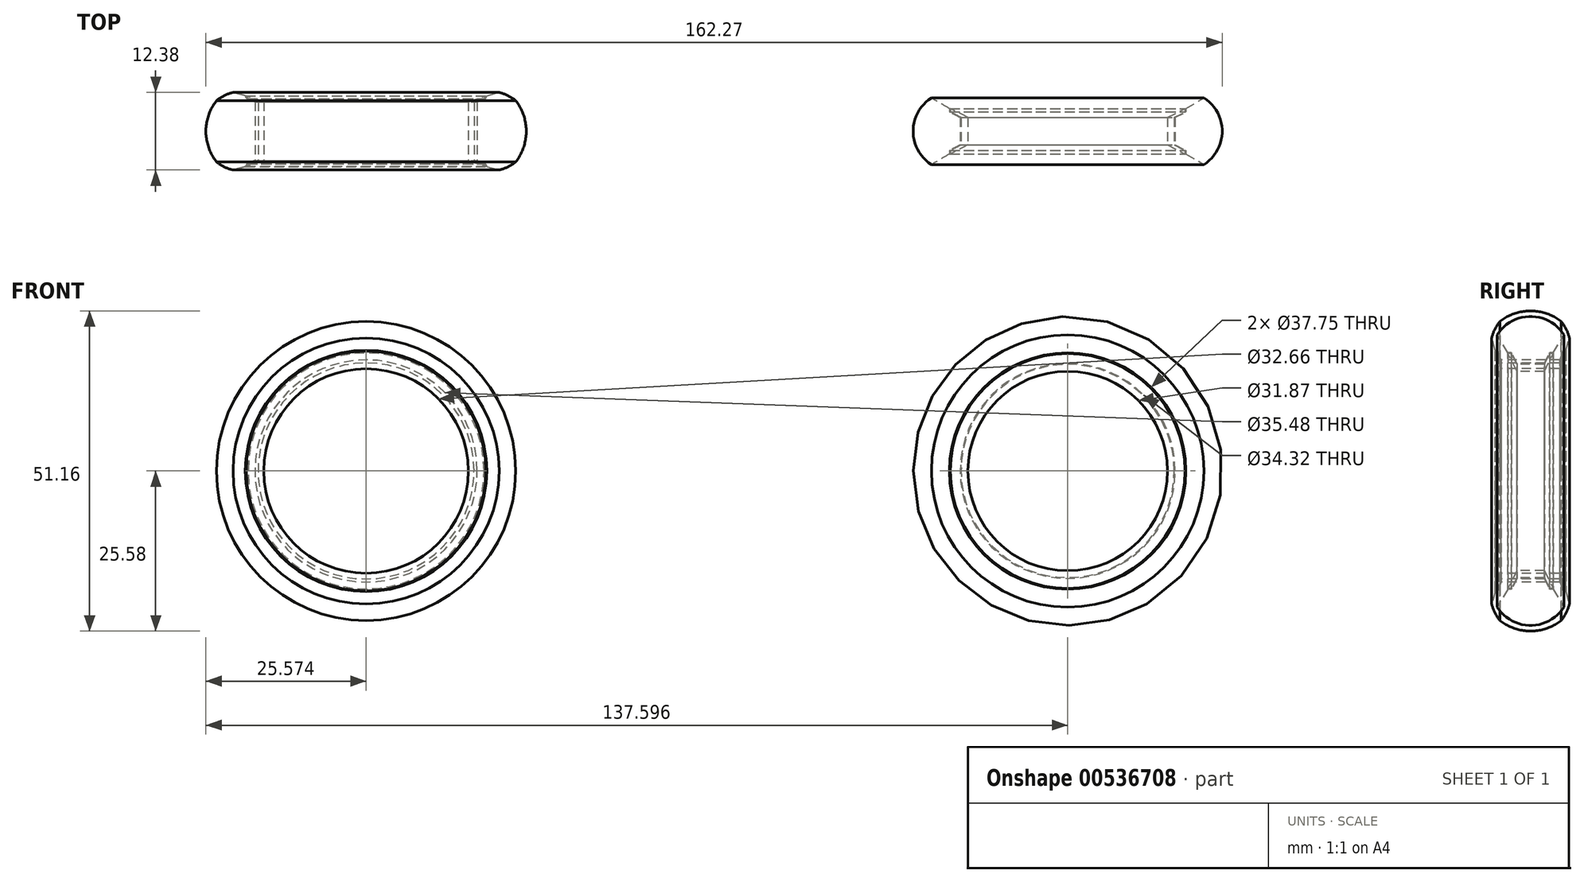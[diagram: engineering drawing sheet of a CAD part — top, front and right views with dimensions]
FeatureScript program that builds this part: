
annotation { "Feature Type Name" : "Feature", "Feature Type Description" : "" }
export const myFeature = defineFeature(function(context is Context, id is Id, definition is map)
    precondition{}
    {
        {
            var Q0;
            Q0=qCreatedBy(makeId("Right.planeOp"),FACE);
            var sketch = newSketch(context, id + "F0", { "sketchPlane" : qUnion([Q0])});
            skLineSegment(sketch, "E0", {"start": v(-44.75, 0) * mm, "end": v(51, 0) * mm, "construction": true});
            skLineSegment(sketch, "E1", {"start": v(-39.14, 41.52) * mm, "end": v(68.46, 41.52) * mm, "construction": true});
            skLineSegment(sketch, "E2", {"start": v(0, 87.56) * mm, "end": v(0, -13.22) * mm, "construction": true});
            skArc(sketch, "E3", {"start": v(5.33, 63.27) * mm, "mid": v(3.04, 65.41) * mm, "end": v(0, 66.19) * mm});
            skLineSegment(sketch, "E4", {"start": v(0, 58.68) * mm, "end": v(2.2, 58.68) * mm});
            skLineSegment(sketch, "E5", {"start": v(2.2, 58.68) * mm, "end": v(3.07, 60.4) * mm});
            skLineSegment(sketch, "E6", {"start": v(3.07, 60.4) * mm, "end": v(3.63, 60.4) * mm});
            skLineSegment(sketch, "E7", {"start": v(3.63, 60.4) * mm, "end": v(5.33, 63.27) * mm});
            skLineSegment(sketch, "E8", {"start": v(0, 58.54) * mm, "end": v(2.2, 58.54) * mm});
            skLineSegment(sketch, "E9", {"start": v(2.2, 58.54) * mm, "end": v(3.07, 60.25) * mm});
            skLineSegment(sketch, "E10", {"start": v(3.07, 60.25) * mm, "end": v(3.63, 60.25) * mm});
            skLineSegment(sketch, "E11", {"start": v(3.63, 60.25) * mm, "end": v(2.2, 57.45) * mm});
            skLineSegment(sketch, "E12", {"start": v(2.2, 57.45) * mm, "end": v(0, 57.45) * mm});
            skArc(sketch, "E13.MirrorCS", {"start": v(-5.33, 63.27) * mm, "mid": v(-3.04, 65.41) * mm, "end": v(0, 66.19) * mm});
            skLineSegment(sketch, "E14.MirrorCS", {"start": v(-3.07, 60.4) * mm, "end": v(-3.63, 60.4) * mm});
            skLineSegment(sketch, "E15.MirrorCS", {"start": v(-3.63, 60.4) * mm, "end": v(-5.33, 63.27) * mm});
            skLineSegment(sketch, "E16.MirrorCS", {"start": v(-3.07, 60.25) * mm, "end": v(-3.63, 60.25) * mm});
            skLineSegment(sketch, "E17.MirrorCS", {"start": v(-3.63, 60.25) * mm, "end": v(-2.2, 57.45) * mm});
            skLineSegment(sketch, "E18.MirrorCS", {"start": v(-2.2, 58.54) * mm, "end": v(-3.07, 60.25) * mm});
            skLineSegment(sketch, "E19.MirrorCS", {"start": v(-2.2, 58.68) * mm, "end": v(-3.07, 60.4) * mm});
            skLineSegment(sketch, "E20.MirrorCS", {"start": v(0, 58.68) * mm, "end": v(-2.2, 58.68) * mm});
            skLineSegment(sketch, "E21.MirrorCS", {"start": v(0, 58.54) * mm, "end": v(-2.2, 58.54) * mm});
            skLineSegment(sketch, "E22.MirrorCS", {"start": v(-2.2, 57.45) * mm, "end": v(0, 57.45) * mm});
            skLineSegment(sketch, "E23", {"start": v(-36.7, -39.4) * mm, "end": v(34, -39.4) * mm, "construction": true});
            skArc(sketch, "E24", {"start": v(6.2, -18.16) * mm, "mid": v(5.7, -16.76) * mm, "end": v(4.88, -15.5) * mm});
            skArc(sketch, "E25", {"start": v(4.88, -15.5) * mm, "mid": v(2.58, -14.27) * mm, "end": v(0, -13.83) * mm});
            skLineSegment(sketch, "E26", {"start": v(6.2, -18.16) * mm, "end": v(5.67, -20.13) * mm});
            skLineSegment(sketch, "E27", {"start": v(5.67, -20.13) * mm, "end": v(5.21, -20.35) * mm});
            skLineSegment(sketch, "E28", {"start": v(5.21, -20.35) * mm, "end": v(4.7, -21.66) * mm});
            skLineSegment(sketch, "E29", {"start": v(4.7, -21.66) * mm, "end": v(0, -21.66) * mm});
            skLineSegment(sketch, "E30", {"start": v(0, -22.16) * mm, "end": v(4.7, -22.16) * mm});
            skLineSegment(sketch, "E31", {"start": v(4.7, -22.16) * mm, "end": v(5.21, -20.57) * mm});
            skLineSegment(sketch, "E32", {"start": v(5.21, -20.57) * mm, "end": v(5.62, -20.27) * mm});
            skLineSegment(sketch, "E33", {"start": v(5.62, -20.27) * mm, "end": v(4.7, -23.08) * mm});
            skLineSegment(sketch, "E34", {"start": v(4.7, -23.08) * mm, "end": v(0, -23.08) * mm});
            skLineSegment(sketch, "E35.trimOffspring", {"start": v(0, -13.83) * mm, "end": v(0, -66.36) * mm, "construction": true});
            skArc(sketch, "E36.MirrorCS", {"start": v(-4.88, -15.5) * mm, "mid": v(-2.58, -14.27) * mm, "end": v(0, -13.83) * mm});
            skArc(sketch, "E37.MirrorCS", {"start": v(-6.2, -18.16) * mm, "mid": v(-5.7, -16.76) * mm, "end": v(-4.88, -15.5) * mm});
            skLineSegment(sketch, "E38.MirrorCS", {"start": v(-5.62, -20.27) * mm, "end": v(-4.7, -23.08) * mm});
            skLineSegment(sketch, "E39.MirrorCS", {"start": v(-4.7, -23.08) * mm, "end": v(0, -23.08) * mm});
            skLineSegment(sketch, "E40.MirrorCS", {"start": v(0, -22.16) * mm, "end": v(-4.7, -22.16) * mm});
            skLineSegment(sketch, "E41.MirrorCS", {"start": v(-4.7, -21.66) * mm, "end": v(0, -21.66) * mm});
            skLineSegment(sketch, "E42.MirrorCS", {"start": v(-6.2, -18.16) * mm, "end": v(-5.67, -20.13) * mm});
            skLineSegment(sketch, "E43.MirrorCS", {"start": v(-4.7, -22.16) * mm, "end": v(-5.21, -20.57) * mm});
            skLineSegment(sketch, "E44.MirrorCS", {"start": v(-5.21, -20.35) * mm, "end": v(-4.7, -21.66) * mm});
            skLineSegment(sketch, "E45.MirrorCS", {"start": v(-5.67, -20.13) * mm, "end": v(-5.21, -20.35) * mm});
            skLineSegment(sketch, "E46.MirrorCS", {"start": v(-5.21, -20.57) * mm, "end": v(-5.62, -20.27) * mm});
            skSolve(sketch);
        }
        {
            var Q0;
            Q0=makeQuery(id+"F0.imprint","IMPRINT",FACE,{"disambiguationData":[TD([[makeQuery(id+"F0.imprint","IMPRINT",EDGE,{"derivedFrom":sQuery(id+"F0.wireOp",EDGE,"E3")}),1.0]])]});
            var Q1;
            Q1=makeQuery(id+"F0.imprint","IMPRINT",FACE,{"disambiguationData":[TD([[makeQuery(id+"F0.imprint","IMPRINT",EDGE,{"derivedFrom":sQuery(id+"F0.wireOp",EDGE,"E8")}),-1.0]])]});
            var Q2;
            Q2=sQuery(id+"F0.wireOp",EDGE,"E1");
            revolve(context, id + "F1", {"entities" : qUnion([Q0, Q1]), "axis" : qUnion([Q2]), "revolveType" : RevolveType.FULL});
        }
        {
            var Q0;
            Q0=makeQuery(id+"F0.imprint","IMPRINT",FACE,{"disambiguationData":[TD([[makeQuery(id+"F0.imprint","IMPRINT",EDGE,{"derivedFrom":sQuery(id+"F0.wireOp",EDGE,"E24")}),1.0]])]});
            var Q1;
            Q1=makeQuery(id+"F0.imprint","IMPRINT",FACE,{"disambiguationData":[TD([[makeQuery(id+"F0.imprint","IMPRINT",EDGE,{"derivedFrom":sQuery(id+"F0.wireOp",EDGE,"E30")}),-1.0]])]});
            var Q2;
            Q2=sQuery(id+"F0.wireOp",EDGE,"E23");
            revolve(context, id + "F2", {"entities" : qUnion([Q0, Q1]), "axis" : qUnion([Q2]), "revolveType" : RevolveType.FULL});
        }
        {
            var Q0;
            Q0=makeQuery(id+"F2.opRevolve","SWEPT_BODY",BODY,{"disambiguationData":[OSD([sQuery(id+"F0.wireOp",EDGE,"E24"),sQuery(id+"F0.wireOp",EDGE,"E25"),sQuery(id+"F0.wireOp",EDGE,"E26"),sQuery(id+"F0.wireOp",EDGE,"E27"),sQuery(id+"F0.wireOp",EDGE,"E28"),sQuery(id+"F0.wireOp",EDGE,"E29"),sQuery(id+"F0.wireOp",EDGE,"E36.MirrorCS"),sQuery(id+"F0.wireOp",EDGE,"E37.MirrorCS"),sQuery(id+"F0.wireOp",EDGE,"E41.MirrorCS"),sQuery(id+"F0.wireOp",EDGE,"E42.MirrorCS"),sQuery(id+"F0.wireOp",EDGE,"E44.MirrorCS"),sQuery(id+"F0.wireOp",EDGE,"E45.MirrorCS")])]});
            var Q1;
            Q1=makeQuery(id+"F2.opRevolve","SWEPT_BODY",BODY,{"disambiguationData":[OSD([sQuery(id+"F0.wireOp",EDGE,"E30"),sQuery(id+"F0.wireOp",EDGE,"E31"),sQuery(id+"F0.wireOp",EDGE,"E32"),sQuery(id+"F0.wireOp",EDGE,"E33"),sQuery(id+"F0.wireOp",EDGE,"E34"),sQuery(id+"F0.wireOp",EDGE,"E38.MirrorCS"),sQuery(id+"F0.wireOp",EDGE,"E39.MirrorCS"),sQuery(id+"F0.wireOp",EDGE,"E40.MirrorCS"),sQuery(id+"F0.wireOp",EDGE,"E43.MirrorCS"),sQuery(id+"F0.wireOp",EDGE,"E46.MirrorCS")])]});
            var Q2;
            Q2=sQuery(id+"F0.wireOp",EDGE,"E2");
            transform(context, id + "F3", {"entities" : qUnion([Q0, Q1]), "transformType" : TransformType.TRANSLATION_DISTANCE, "transformDirection" : qUnion([Q2]), "distance" : 31.1 * mm, "makeCopy" : false});
        }
        {
            var Q0;
            Q0=makeQuery(id+"F2.opRevolve","SWEPT_BODY",BODY,{"disambiguationData":[OSD([sQuery(id+"F0.wireOp",EDGE,"E24"),sQuery(id+"F0.wireOp",EDGE,"E25"),sQuery(id+"F0.wireOp",EDGE,"E26"),sQuery(id+"F0.wireOp",EDGE,"E27"),sQuery(id+"F0.wireOp",EDGE,"E28"),sQuery(id+"F0.wireOp",EDGE,"E29"),sQuery(id+"F0.wireOp",EDGE,"E36.MirrorCS"),sQuery(id+"F0.wireOp",EDGE,"E37.MirrorCS"),sQuery(id+"F0.wireOp",EDGE,"E41.MirrorCS"),sQuery(id+"F0.wireOp",EDGE,"E42.MirrorCS"),sQuery(id+"F0.wireOp",EDGE,"E44.MirrorCS"),sQuery(id+"F0.wireOp",EDGE,"E45.MirrorCS")])]});
            var Q1;
            Q1=makeQuery(id+"F1.opRevolve","SWEPT_BODY",BODY,{"disambiguationData":[OSD([sQuery(id+"F0.wireOp",EDGE,"E8"),sQuery(id+"F0.wireOp",EDGE,"E9"),sQuery(id+"F0.wireOp",EDGE,"E10"),sQuery(id+"F0.wireOp",EDGE,"E11"),sQuery(id+"F0.wireOp",EDGE,"E12"),sQuery(id+"F0.wireOp",EDGE,"E16.MirrorCS"),sQuery(id+"F0.wireOp",EDGE,"E17.MirrorCS"),sQuery(id+"F0.wireOp",EDGE,"E18.MirrorCS"),sQuery(id+"F0.wireOp",EDGE,"E21.MirrorCS"),sQuery(id+"F0.wireOp",EDGE,"E22.MirrorCS")])]});
            var Q2;
            Q2=makeQuery(id+"F1.opRevolve","SWEPT_BODY",BODY,{"disambiguationData":[OSD([sQuery(id+"F0.wireOp",EDGE,"E3"),sQuery(id+"F0.wireOp",EDGE,"E4"),sQuery(id+"F0.wireOp",EDGE,"E5"),sQuery(id+"F0.wireOp",EDGE,"E6"),sQuery(id+"F0.wireOp",EDGE,"E7"),sQuery(id+"F0.wireOp",EDGE,"E13.MirrorCS"),sQuery(id+"F0.wireOp",EDGE,"E15.MirrorCS"),sQuery(id+"F0.wireOp",EDGE,"E14.MirrorCS"),sQuery(id+"F0.wireOp",EDGE,"E19.MirrorCS"),sQuery(id+"F0.wireOp",EDGE,"E20.MirrorCS")])]});
            var Q3;
            Q3=makeQuery(id+"F2.opRevolve","SWEPT_BODY",BODY,{"disambiguationData":[OSD([sQuery(id+"F0.wireOp",EDGE,"E30"),sQuery(id+"F0.wireOp",EDGE,"E31"),sQuery(id+"F0.wireOp",EDGE,"E32"),sQuery(id+"F0.wireOp",EDGE,"E33"),sQuery(id+"F0.wireOp",EDGE,"E34"),sQuery(id+"F0.wireOp",EDGE,"E38.MirrorCS"),sQuery(id+"F0.wireOp",EDGE,"E39.MirrorCS"),sQuery(id+"F0.wireOp",EDGE,"E40.MirrorCS"),sQuery(id+"F0.wireOp",EDGE,"E43.MirrorCS"),sQuery(id+"F0.wireOp",EDGE,"E46.MirrorCS")])]});
            var Q4;
            Q4=sQuery(id+"F0.wireOp",EDGE,"E0");
            transform(context, id + "F4", {"entities" : qUnion([Q0, Q1, Q2, Q3]), "transformType" : TransformType.ROTATION, "transformAxis" : qUnion([Q4]), "angle" : 90 * degree, "makeCopy" : false});
        }
    });
